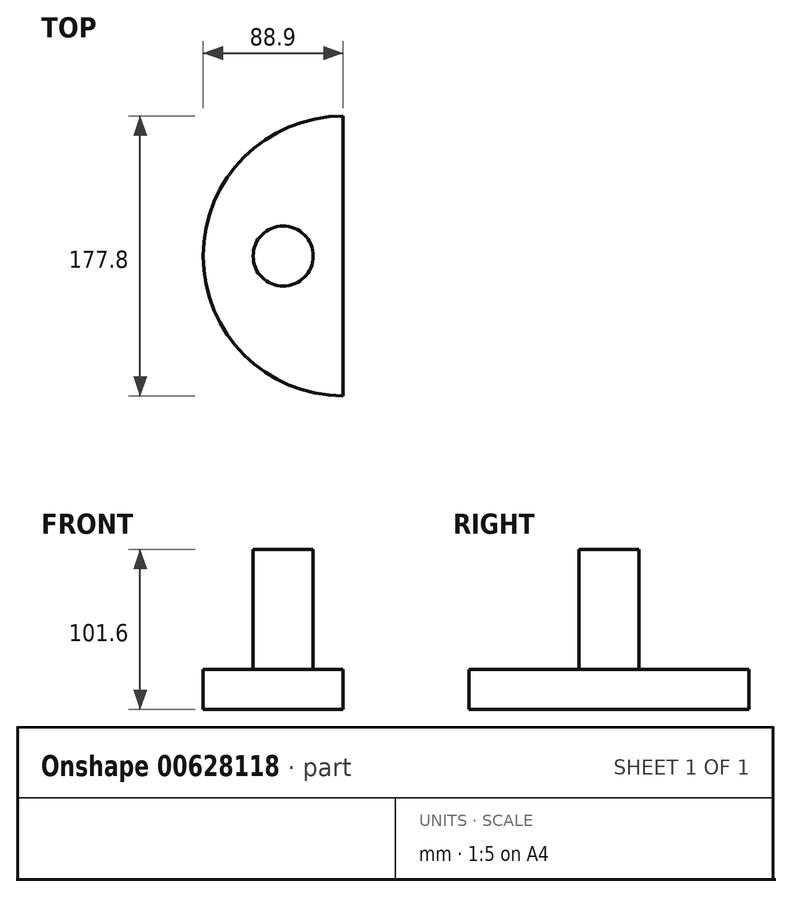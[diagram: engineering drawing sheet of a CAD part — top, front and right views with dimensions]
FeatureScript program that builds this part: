
annotation { "Feature Type Name" : "Feature", "Feature Type Description" : "" }
export const myFeature = defineFeature(function(context is Context, id is Id, definition is map)
    precondition{}
    {
        {
            var Q0;
            Q0=qCreatedBy(makeId("Top.planeOp"),FACE);
            var sketch = newSketch(context, id + "F0", { "sketchPlane" : qUnion([Q0])});
            skArc(sketch, "E0", {"start": v(0, 88.9) * mm, "mid": v(-88.9, 0) * mm, "end": v(0, -88.9) * mm});
            skLineSegment(sketch, "E1", {"start": v(0, 88.9) * mm, "end": v(0, -88.9) * mm});
            skCircle(sketch, "E2", {"center": v(-38.1, 0) * mm, "radius": 19.05 * mm});
            skSolve(sketch);
        }
        {
            var Q0;
            Q0=makeQuery(id+"F0.imprint","IMPRINT",FACE,{"disambiguationData":[TD([[makeQuery(id+"F0.imprint","IMPRINT",EDGE,{"derivedFrom":sQuery(id+"F0.wireOp",EDGE,"E2")}),1.0]])]});
            extrude(context, id + "F1", {"entities" : qUnion([Q0]), "depth" : 101.6 * mm, "offsetDistance" : 25.4 * mm});
        }
        {
            var Q0;
            Q0=makeQuery(id+"F0.imprint","IMPRINT",FACE,{"disambiguationData":[TD([[makeQuery(id+"F0.imprint","IMPRINT",EDGE,{"derivedFrom":sQuery(id+"F0.wireOp",EDGE,"E0")}),1.0]])]});
            extrude(context, id + "F2", {"entities" : qUnion([Q0]), "operationType" : NewBodyOperationType.ADD, "depth" : 25.4 * mm, "offsetDistance" : 25.4 * mm});
        }
        {
            var Q0;
            Q0=makeQuery(id+"F1.opExtrude","CAP_FACE",FACE,{"disambiguationData":[OSD([sQuery(id+"F0.wireOp",EDGE,"E2")])],"isStart":false});
            extrude(context, id + "F3", {"entities" : qUnion([Q0]), "operationType" : NewBodyOperationType.REMOVE, "depth" : 76.2 * mm, "offsetDistance" : 25.4 * mm});
        }
    });
